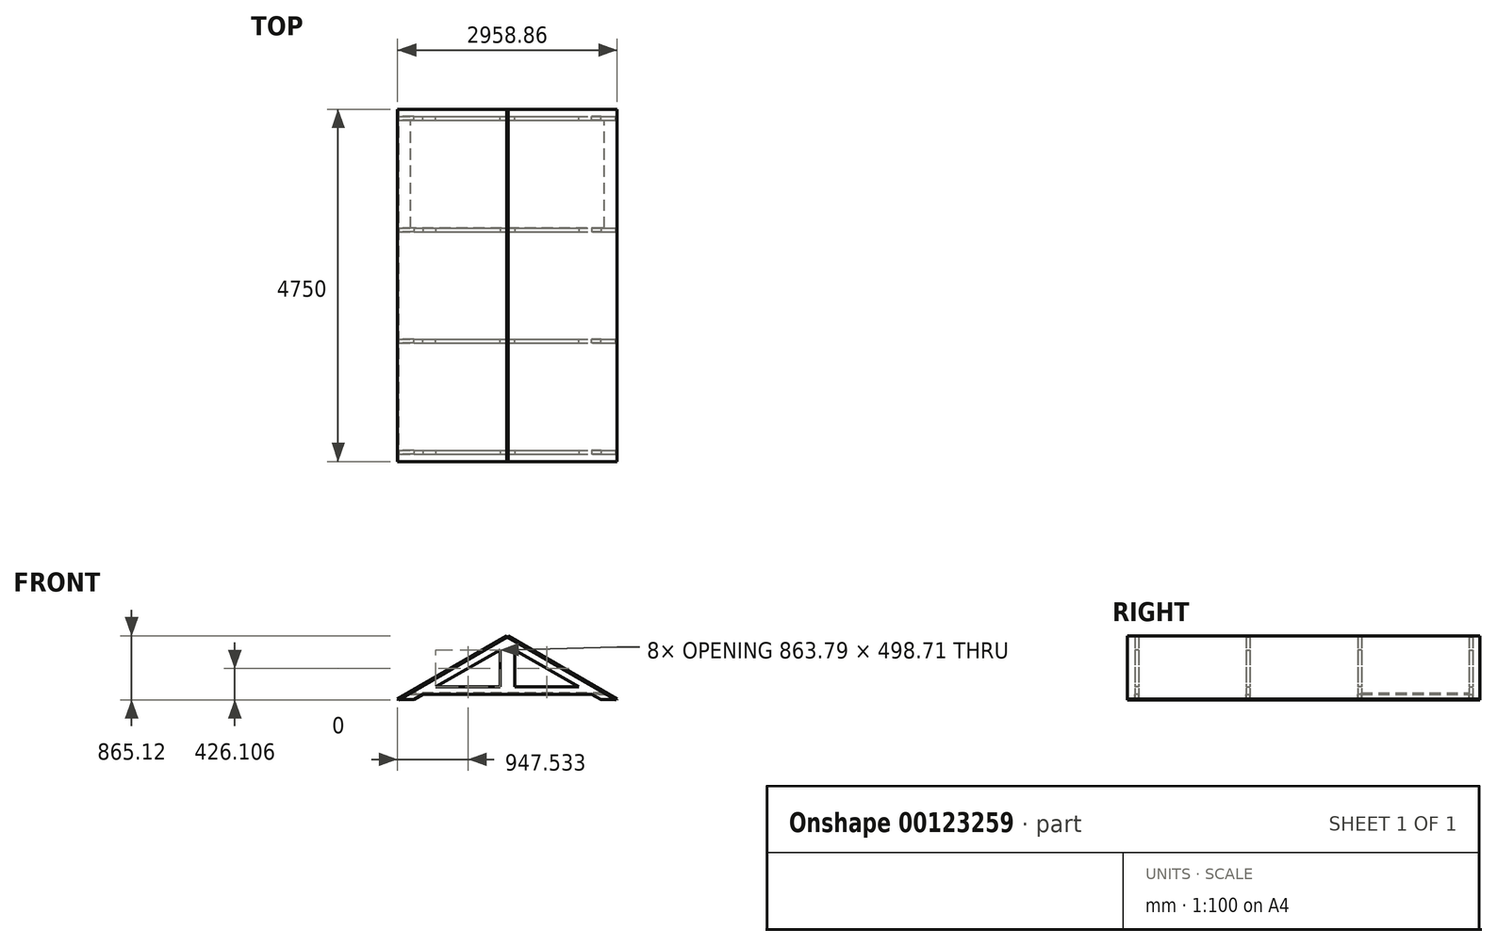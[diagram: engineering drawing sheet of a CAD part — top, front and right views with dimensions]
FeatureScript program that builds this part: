
annotation { "Feature Type Name" : "Feature", "Feature Type Description" : "" }
export const myFeature = defineFeature(function(context is Context, id is Id, definition is map)
    precondition{}
    {
        {
            var Q0;
            Q0=qCreatedBy(makeId("Front.planeOp"),FACE);
            var sketch = newSketch(context, id + "F0", { "sketchPlane" : qUnion([Q0])});
            skLineSegment(sketch, "E0", {"start": v(-1137, 0) * mm, "end": v(0, 656.45) * mm});
            skLineSegment(sketch, "E1", {"start": v(0, 656.45) * mm, "end": v(1137, 0) * mm});
            skLineSegment(sketch, "E2", {"start": v(-963.8, 100) * mm, "end": v(963.8, 100) * mm});
            skLineSegment(sketch, "E3", {"start": v(0, 656.45) * mm, "end": v(0, 100) * mm});
            skLineSegment(sketch, "E4", {"start": v(0, 100) * mm, "end": v(100, 100) * mm});
            skLineSegment(sketch, "E5", {"start": v(100, 100) * mm, "end": v(100, 598.71) * mm});
            skLineSegment(sketch, "E6.MirrorCS", {"start": v(-100, 100) * mm, "end": v(-100, 598.71) * mm});
            skLineSegment(sketch, "E7", {"start": v(-1337, 0) * mm, "end": v(0, 771.92) * mm});
            skLineSegment(sketch, "E8", {"start": v(0, 656.45) * mm, "end": v(0, 771.92) * mm});
            skLineSegment(sketch, "E9", {"start": v(-1337, 0) * mm, "end": v(-1461.27, -71.75) * mm});
            skLineSegment(sketch, "E10", {"start": v(-1261.27, -71.75) * mm, "end": v(-1461.27, -71.75) * mm});
            skPoint(sketch, "E11.start.orphan", {"position": v(-1137, 0) * mm});
            skLineSegment(sketch, "E12", {"start": v(-1261.27, -71.75) * mm, "end": v(-1137, 0) * mm});
            skLineSegment(sketch, "E13.MirrorCS", {"start": v(1337, 0) * mm, "end": v(0, 771.92) * mm});
            skLineSegment(sketch, "E14.MirrorCS", {"start": v(1137, 0) * mm, "end": v(0, 656.45) * mm});
            skLineSegment(sketch, "E15.MirrorCS", {"start": v(1261.27, -71.75) * mm, "end": v(1461.27, -71.75) * mm});
            skLineSegment(sketch, "E16.MirrorCS", {"start": v(1337, 0) * mm, "end": v(1461.27, -71.75) * mm});
            skLineSegment(sketch, "E17.MirrorCS", {"start": v(1261.27, -71.75) * mm, "end": v(1137, 0) * mm});
            skLineSegment(sketch, "E18", {"start": v(-1137, 0) * mm, "end": v(1137, 0) * mm});
            skSolve(sketch);
        }
        {
            var Q0;
            Q0 = qSketchRegion(id + "F0", true);
            var Q1;
            {var subQ0=sQuery(id+"F0.wireOp",EDGE,"E3");Q1=makeQuery(id+"F0.imprint","IMPRINT",FACE,{"disambiguationData":[TD([[makeQuery(id+"F0.imprint","IMPRINT",EDGE,{"derivedFrom":subQ0}),-1.0]])]});}
            var Q2;
            {var subQ0=sQuery(id+"F0.wireOp",EDGE,"E3");Q2=makeQuery(id+"F0.imprint","IMPRINT",FACE,{"disambiguationData":[TD([[makeQuery(id+"F0.imprint","IMPRINT",EDGE,{"derivedFrom":subQ0}),1.0]])]});}
            extrude(context, id + "F1", {"entities" : qUnion([Q0, Q1, Q2]), "endBound" : BoundingType.SYMMETRIC, "depth" : 50 * mm});
        }
        {
            var Q0;
            Q0=qCreatedBy(makeId("Front.planeOp"),FACE);
            cPlane(context, id + "F2", {"entities" : qUnion([Q0]), "cplaneType" : CPlaneType.OFFSET, "offset" : 750 * mm, "width" : 150 * mm, "height" : 150 * mm});
        }
        {
            var Q0;
            Q0=makeQuery(id+"F1.opExtrude","SWEPT_BODY",BODY,{"disambiguationData":[OSD([sQuery(id+"F0.wireOp",EDGE,"E0"),sQuery(id+"F0.wireOp",EDGE,"E2"),sQuery(id+"F0.wireOp",EDGE,"E5"),sQuery(id+"F0.wireOp",EDGE,"E6.MirrorCS"),sQuery(id+"F0.wireOp",EDGE,"E7"),sQuery(id+"F0.wireOp",EDGE,"E9"),sQuery(id+"F0.wireOp",EDGE,"E10"),sQuery(id+"F0.wireOp",EDGE,"E12"),sQuery(id+"F0.wireOp",EDGE,"frrAzBoH-h8tl-Y416-RTqV-Bgqu27tgJSFN"),sQuery(id+"F0.wireOp",EDGE,"E13.MirrorCS"),sQuery(id+"F0.wireOp",EDGE,"E14.MirrorCS"),sQuery(id+"F0.wireOp",EDGE,"E15.MirrorCS"),sQuery(id+"F0.wireOp",EDGE,"E16.MirrorCS"),sQuery(id+"F0.wireOp",EDGE,"E17.MirrorCS")])]});
            var Q1;
            Q1=qCreatedBy(id+"F2.planeOp",FACE);
            mirror(context, id + "F3", {"entities" : qUnion([Q0]), "mirrorPlane" : qUnion([Q1])});
        }
        {
            var Q0;
            Q0=qCreatedBy(makeId("Front.planeOp"),FACE);
            cPlane(context, id + "F4", {"entities" : qUnion([Q0]), "cplaneType" : CPlaneType.OFFSET, "offset" : 2250 * mm, "width" : 150 * mm, "height" : 150 * mm});
        }
        {
            var Q0;
            Q0=makeQuery(id+"F3.opPattern","COPY",BODY,{"derivedFrom":makeQuery(id+"F1.opExtrude","SWEPT_BODY",BODY,{"disambiguationData":[OSD([sQuery(id+"F0.wireOp",EDGE,"E0"),sQuery(id+"F0.wireOp",EDGE,"E2"),sQuery(id+"F0.wireOp",EDGE,"E5"),sQuery(id+"F0.wireOp",EDGE,"E6.MirrorCS"),sQuery(id+"F0.wireOp",EDGE,"E7"),sQuery(id+"F0.wireOp",EDGE,"E9"),sQuery(id+"F0.wireOp",EDGE,"E10"),sQuery(id+"F0.wireOp",EDGE,"E12"),sQuery(id+"F0.wireOp",EDGE,"frrAzBoH-h8tl-Y416-RTqV-Bgqu27tgJSFN"),sQuery(id+"F0.wireOp",EDGE,"E13.MirrorCS"),sQuery(id+"F0.wireOp",EDGE,"E14.MirrorCS"),sQuery(id+"F0.wireOp",EDGE,"E15.MirrorCS"),sQuery(id+"F0.wireOp",EDGE,"E16.MirrorCS"),sQuery(id+"F0.wireOp",EDGE,"E17.MirrorCS")])]}),"instanceName":"1"});
            var Q1;
            Q1=makeQuery(id+"F1.opExtrude","SWEPT_BODY",BODY,{"disambiguationData":[OSD([sQuery(id+"F0.wireOp",EDGE,"E0"),sQuery(id+"F0.wireOp",EDGE,"E2"),sQuery(id+"F0.wireOp",EDGE,"E5"),sQuery(id+"F0.wireOp",EDGE,"E6.MirrorCS"),sQuery(id+"F0.wireOp",EDGE,"E7"),sQuery(id+"F0.wireOp",EDGE,"E9"),sQuery(id+"F0.wireOp",EDGE,"E10"),sQuery(id+"F0.wireOp",EDGE,"E12"),sQuery(id+"F0.wireOp",EDGE,"frrAzBoH-h8tl-Y416-RTqV-Bgqu27tgJSFN"),sQuery(id+"F0.wireOp",EDGE,"E13.MirrorCS"),sQuery(id+"F0.wireOp",EDGE,"E14.MirrorCS"),sQuery(id+"F0.wireOp",EDGE,"E15.MirrorCS"),sQuery(id+"F0.wireOp",EDGE,"E16.MirrorCS"),sQuery(id+"F0.wireOp",EDGE,"E17.MirrorCS")])]});
            var Q2;
            Q2=qCreatedBy(id+"F4.planeOp",FACE);
            mirror(context, id + "F5", {"entities" : qUnion([Q0, Q1]), "mirrorPlane" : qUnion([Q2])});
        }
        {
            var Q0;
            Q0=qCreatedBy(makeId("Right.planeOp"),FACE);
            var Q1;
            Q1=makeQuery(id+"F5.opPattern","COPY",EDGE,{"derivedFrom":makeQuery(id+"F1.opExtrude","CAP_EDGE",EDGE,{"disambiguationData":[OSD([sQuery(id+"F0.wireOp",EDGE,"E7"),sQuery(id+"F0.wireOp",EDGE,"E9")])],"isStart":true}),"instanceName":"1"});
            cPlane(context, id + "F6", {"entities" : qUnion([Q0, Q1]), "cplaneType" : CPlaneType.LINE_ANGLE, "offset" : 25 * mm, "angle" : 0 * degree, "width" : 150 * mm, "height" : 150 * mm});
        }
        {
            var Q0;
            Q0=qCreatedBy(id+"F6.planeOp",FACE);
            var sketch = newSketch(context, id + "F7", { "sketchPlane" : qUnion([Q0])});
            skLineSegment(sketch, "E19.bottom", {"start": v(-1311.37, 125) * mm, "end": v(385.96, 125) * mm});
            skLineSegment(sketch, "E19.top", {"start": v(-1311.37, -4625) * mm, "end": v(385.96, -4625) * mm});
            skLineSegment(sketch, "E19.left", {"start": v(-1311.37, 125) * mm, "end": v(-1311.37, -4625) * mm});
            skLineSegment(sketch, "E19.right", {"start": v(385.96, 125) * mm, "end": v(385.96, -4625) * mm});
            skSolve(sketch);
        }
        {
            var Q0;
            Q0=makeQuery(id+"F7.imprint","IMPRINT",FACE,{"disambiguationData":[TD([[makeQuery(id+"F7.imprint","IMPRINT",EDGE,{"derivedFrom":sQuery(id+"F7.wireOp",EDGE,"E19.bottom")}),-1.0]])]});
            extrude(context, id + "F8", {"entities" : qUnion([Q0]), "depth" : 19 * mm});
        }
        {
            var Q0;
            Q0=makeQuery(id+"F8.opExtrude","SWEPT_BODY",BODY,{"disambiguationData":[OSD([sQuery(id+"F7.wireOp",EDGE,"E19.bottom"),sQuery(id+"F7.wireOp",EDGE,"E19.top"),sQuery(id+"F7.wireOp",EDGE,"E19.left"),sQuery(id+"F7.wireOp",EDGE,"E19.right")])]});
            var Q1;
            Q1=qCreatedBy(makeId("Right.planeOp"),FACE);
            mirror(context, id + "F9", {"entities" : qUnion([Q0]), "mirrorPlane" : qUnion([Q1])});
        }
        {
            var Q0;
            Q0=qCreatedBy(id+"F2.planeOp",FACE);
            var sketch = newSketch(context, id + "F10", { "sketchPlane" : qUnion([Q0])});
            skLineSegment(sketch, "E20.bottom", {"start": v(-1137, 0) * mm, "end": v(1136.16, 0) * mm});
            skLineSegment(sketch, "E20.top", {"start": v(-1137, 20) * mm, "end": v(1136.16, 20) * mm});
            skLineSegment(sketch, "E21", {"start": v(-1137, 20) * mm, "end": v(-1302.52, 20) * mm});
            skLineSegment(sketch, "E22", {"start": v(-1302.52, 20) * mm, "end": v(-1302.52, 0) * mm});
            skLineSegment(sketch, "E23", {"start": v(-1302.52, 0) * mm, "end": v(-1137, 0) * mm});
            skLineSegment(sketch, "E24", {"start": v(1136.16, 20) * mm, "end": v(1303.76, 20) * mm});
            skLineSegment(sketch, "E25", {"start": v(1303.76, 20) * mm, "end": v(1303.76, 0) * mm});
            skLineSegment(sketch, "E26", {"start": v(1136.16, 0) * mm, "end": v(1303.76, 0) * mm});
            skSolve(sketch);
        }
        {
            var Q0;
            Q0=makeQuery(id+"F10.imprint","IMPRINT",FACE,{"disambiguationData":[TD([[makeQuery(id+"F10.imprint","IMPRINT",EDGE,{"derivedFrom":sQuery(id+"F10.wireOp",EDGE,"E20.bottom")}),1.0]])]});
            var Q1;
            Q1=makeQuery(id+"F3.opPattern","COPY",FACE,{"derivedFrom":makeQuery(id+"F1.opExtrude","CAP_FACE",FACE,{"disambiguationData":[OSD([sQuery(id+"F0.wireOp",EDGE,"E0"),sQuery(id+"F0.wireOp",EDGE,"E2"),sQuery(id+"F0.wireOp",EDGE,"E5"),sQuery(id+"F0.wireOp",EDGE,"E6.MirrorCS"),sQuery(id+"F0.wireOp",EDGE,"E7"),sQuery(id+"F0.wireOp",EDGE,"E9"),sQuery(id+"F0.wireOp",EDGE,"E10"),sQuery(id+"F0.wireOp",EDGE,"E12"),sQuery(id+"F0.wireOp",EDGE,"E13.MirrorCS"),sQuery(id+"F0.wireOp",EDGE,"E14.MirrorCS"),sQuery(id+"F0.wireOp",EDGE,"E15.MirrorCS"),sQuery(id+"F0.wireOp",EDGE,"E16.MirrorCS"),sQuery(id+"F0.wireOp",EDGE,"E17.MirrorCS"),sQuery(id+"F0.wireOp",EDGE,"E18")])],"isStart":false}),"instanceName":"1"});
            var Q2;
            Q2=makeQuery(id+"F1.opExtrude","CAP_FACE",FACE,{"disambiguationData":[OSD([sQuery(id+"F0.wireOp",EDGE,"E0"),sQuery(id+"F0.wireOp",EDGE,"E2"),sQuery(id+"F0.wireOp",EDGE,"E5"),sQuery(id+"F0.wireOp",EDGE,"E6.MirrorCS"),sQuery(id+"F0.wireOp",EDGE,"E7"),sQuery(id+"F0.wireOp",EDGE,"E9"),sQuery(id+"F0.wireOp",EDGE,"E10"),sQuery(id+"F0.wireOp",EDGE,"E12"),sQuery(id+"F0.wireOp",EDGE,"E13.MirrorCS"),sQuery(id+"F0.wireOp",EDGE,"E14.MirrorCS"),sQuery(id+"F0.wireOp",EDGE,"E15.MirrorCS"),sQuery(id+"F0.wireOp",EDGE,"E16.MirrorCS"),sQuery(id+"F0.wireOp",EDGE,"E17.MirrorCS"),sQuery(id+"F0.wireOp",EDGE,"E18")])],"isStart":false});
            extrude(context, id + "F11", {"entities" : qUnion([Q0]), "endBound" : BoundingType.UP_TO_SURFACE, "endBoundEntityFace" : qUnion([Q1]), "depth" : 25 * mm, "hasSecondDirection" : true, "secondDirectionBound" : SecondDirectionBoundingType.UP_TO_SURFACE, "secondDirectionOppositeDirection" : true, "secondDirectionBoundEntityFace" : qUnion([Q2]), "secondDirectionDepth" : 25 * mm});
        }
    });
